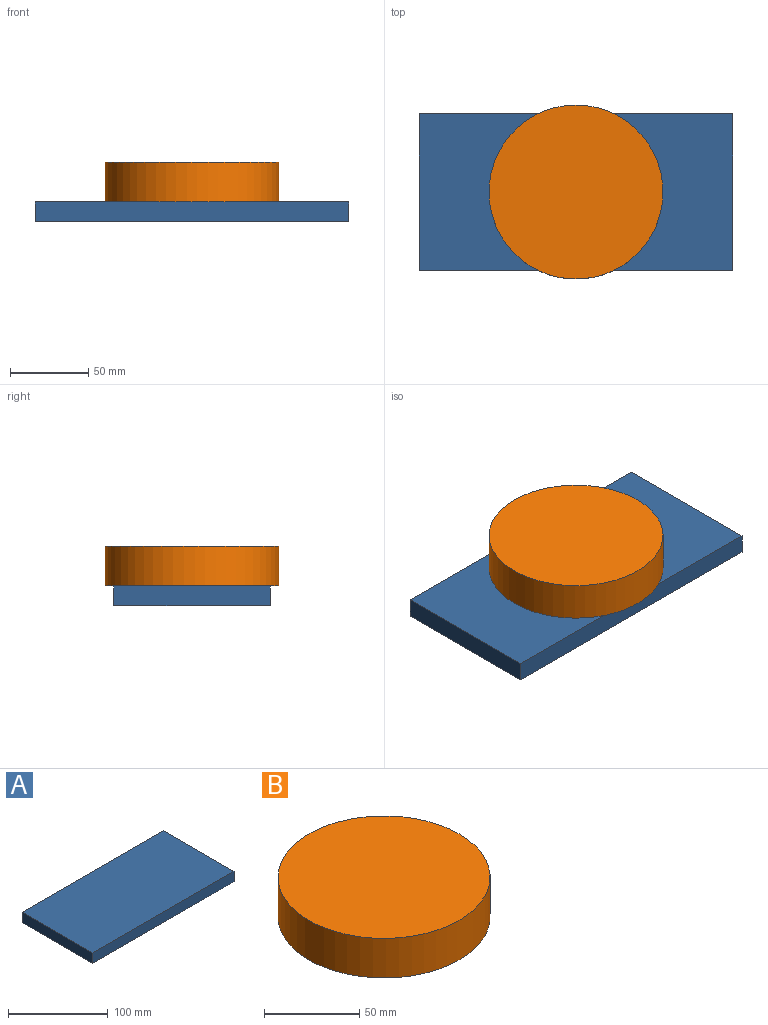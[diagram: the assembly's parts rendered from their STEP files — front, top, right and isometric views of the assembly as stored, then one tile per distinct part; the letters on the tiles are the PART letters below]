
ASSEMBLY  parts=2 mates=1
PART A: 6 faces, bbox 200x100x12.7 mm
  f0: plane 100x12.7mm, normal (1,0,0), area 1270mm2, adj f1,f3,f4,f5
  f1: plane 200x12.7mm, normal (0,1,0), area 2540mm2, adj f0,f2,f4,f5
  f2: plane 100x12.7mm, normal (-1,0,0), area 1270mm2, adj f1,f3,f4,f5
  f3: plane 200x12.7mm, normal (0,-1,0), area 2540mm2, adj f0,f2,f4,f5
  f4: plane 200x100mm, normal (0,0,1), area 20000mm2, adj f0,f1,f2,f3
  f5: plane 200x100mm, normal (0,0,-1), area 20000mm2, adj f0,f1,f2,f3
PART B: 3 faces, bbox 111.2x111.2x25.4 mm
  f0: cylinder r=55.61mm len=111.21mm, axis (0,0,-1), area 8874.4mm2, adj f1,f2
  f1: plane 111.21x111.21mm, normal (0,0,1), area 9714mm2, adj f0
  f2: plane 111.21x111.21mm, normal (0,0,-1), area 9714mm2, adj f0
PLACE A t=(42.89,56.74,39.07)mm
PLACE B rot(axis=(0,0,1),90deg) t=(45.84,56.74,51.77)mm
MATE parallel B.f0 <-> A.f4  axis (0,0,-1) through (45.84,56.74,51.77)mm
